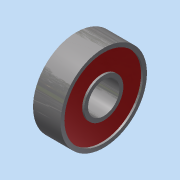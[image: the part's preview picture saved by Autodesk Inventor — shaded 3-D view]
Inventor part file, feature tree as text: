
AUTODESK INVENTOR PART (.ipt)
format: ipt  version: 2015 (Build 190159000, 159)  size: 121,856 bytes
history: native  units: in
note: dims shown in document units (in); Inventor stores cm internally (conversion verified against a paired STEP export)
features: extrude x2, sketch x2, plane x1, mirror x1, projected_geometry x1
ambient origin geometry x8: Origin, YZ Plane, XZ Plane, XY Plane, X Axis, Y Axis, Z Axis, Center Point
bodies: Solid1 (feature_tree)
feature tree (7):
  extrude  "Extrusion1"  Depth=0.8661in
  plane  "Work Plane1"
  extrude  "Extrusion2"  Depth=0.0197in
  mirror  "Mirror1"
  sketch  "Sketch1"  dims[d0=0.315in d1=0.8661in]
  sketch  "Sketch2"  dims[d2=0.2756in d3=0.0in d4=0.0394in d5=0.0394in d6=0.0197in d7=0.0in]
  projected_geometry  "Projected Loop1"
